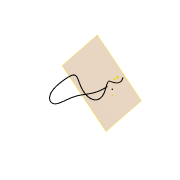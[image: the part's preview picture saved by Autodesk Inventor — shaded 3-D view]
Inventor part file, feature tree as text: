
AUTODESK INVENTOR PART (.ipt)
format: ipt  version: 2022 (Build 260153000, 153)  size: 310,784 bytes
history: native  units: mm
features: other x7, sketch x2, plane x2, sweep x1
ambient origin geometry x8: Origin, YZ Plane, XZ Plane, XY Plane, X Axis, Y Axis, Z Axis, Center Point
bodies: Volumenkörper1 (feature_tree)
feature tree (12):
  other  "3D-Skizze1"
  sketch  "Skizze1"  dims[d0=0.0mm d1=0.0mm]
  plane  "Arbeitsebene2"
  sweep  "Sweeping1"
  other  "Arbeitspunkt1"
  other  "Arbeitspunkt2"
  other  "Arbeitspunkt3"
  plane  "Arbeitsebene1"
  sketch  "Skizze2"
  other  "Anglerfish_bonne_mamman_m12large_flipped_v0.iam"
  other  "00_Coverglass:1"
  other  "Anglerfish_Lightplate_Tosslink_flipped:1"
